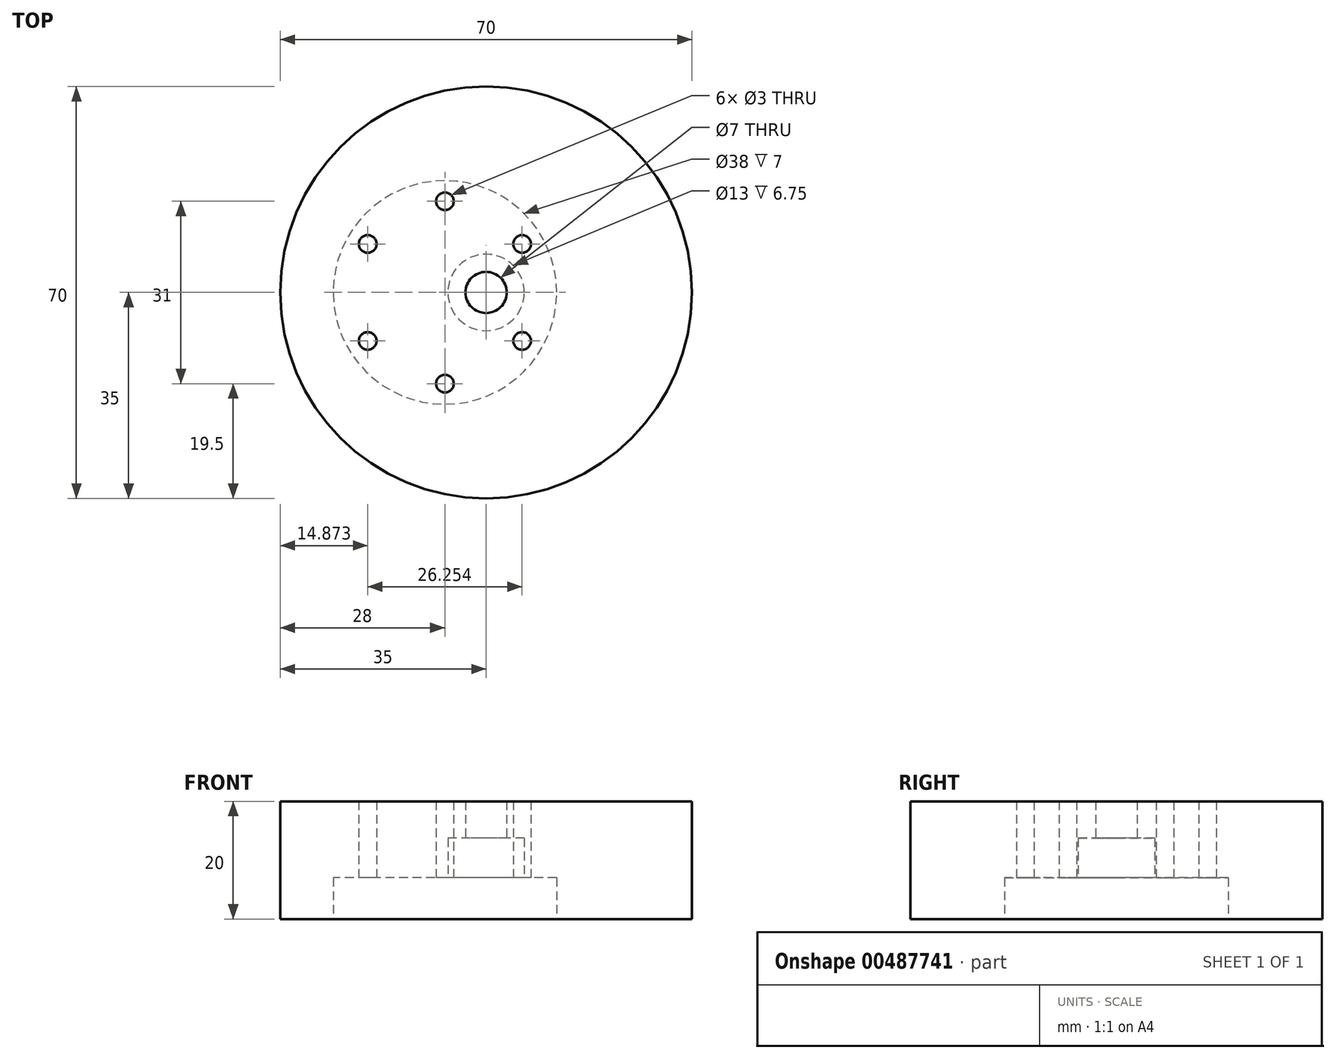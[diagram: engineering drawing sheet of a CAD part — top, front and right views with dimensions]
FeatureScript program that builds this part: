
annotation { "Feature Type Name" : "Feature", "Feature Type Description" : "" }
export const myFeature = defineFeature(function(context is Context, id is Id, definition is map)
    precondition{}
    {
        {
            var Q0;
            Q0=qCreatedBy(makeId("Top.planeOp"),FACE);
            var sketch = newSketch(context, id + "F0", { "sketchPlane" : qUnion([Q0])});
            skCircle(sketch, "E0", {"center": v(0, 0) * mm, "radius": 6.5 * mm});
            skCircle(sketch, "E1", {"center": v(-7, 0) * mm, "radius": 19 * mm});
            skLineSegment(sketch, "E2", {"start": v(-7, 0) * mm, "end": v(0, 0) * mm, "construction": true});
            skCircle(sketch, "E3", {"center": v(0, 0) * mm, "radius": 3.5 * mm});
            skLineSegment(sketch, "E4", {"start": v(-7, 0) * mm, "end": v(-26, 0) * mm, "construction": true});
            skLineSegment(sketch, "E5", {"start": v(-7, -19) * mm, "end": v(-7, 19) * mm, "construction": true});
            skCircle(sketch, "E6", {"center": v(-7, 15.5) * mm, "radius": 1.5 * mm});
            skCircle(sketch, "E7", {"center": v(-7, -15.5) * mm, "radius": 1.5 * mm});
            skCircle(sketch, "E8", {"center": v(-7, 0) * mm, "radius": 15.5 * mm, "construction": true});
            skCircle(sketch, "E9", {"center": v(-20.13, 8.24) * mm, "radius": 1.5 * mm});
            skCircle(sketch, "E10", {"center": v(6.13, -8.24) * mm, "radius": 1.5 * mm});
            skCircle(sketch, "E11", {"center": v(-20.13, -8.24) * mm, "radius": 1.5 * mm});
            skCircle(sketch, "E12", {"center": v(6.13, 8.24) * mm, "radius": 1.5 * mm});
            skLineSegment(sketch, "E13", {"start": v(-20.13, 8.24) * mm, "end": v(6.13, 8.24) * mm, "construction": true});
            skLineSegment(sketch, "E14", {"start": v(-20.13, -8.24) * mm, "end": v(6.13, -8.24) * mm, "construction": true});
            skCircle(sketch, "E15", {"center": v(0, 0) * mm, "radius": 35 * mm});
            skSolve(sketch);
        }
        {
            var Q0;
            Q0=makeQuery(id+"F0.imprint","IMPRINT",FACE,{"disambiguationData":[TD([[makeQuery(id+"F0.imprint","IMPRINT",EDGE,{"derivedFrom":sQuery(id+"F0.wireOp",EDGE,"E1")}),-1.0]])]});
            var Q1;
            Q1=makeQuery(id+"F0.imprint","IMPRINT",FACE,{"disambiguationData":[TD([[makeQuery(id+"F0.imprint","IMPRINT",EDGE,{"derivedFrom":sQuery(id+"F0.wireOp",EDGE,"E0")}),-1.0]])]});
            var Q2;
            Q2=makeQuery(id+"F0.imprint","IMPRINT",FACE,{"disambiguationData":[TD([[makeQuery(id+"F0.imprint","IMPRINT",EDGE,{"derivedFrom":sQuery(id+"F0.wireOp",EDGE,"E0")}),1.0]])]});
            extrude(context, id + "F1", {"entities" : qUnion([Q0, Q1, Q2]), "depth" : 20 * mm});
        }
        {
            var Q0;
            Q0=makeQuery(id+"F0.imprint","IMPRINT",FACE,{"disambiguationData":[TD([[makeQuery(id+"F0.imprint","IMPRINT",EDGE,{"derivedFrom":sQuery(id+"F0.wireOp",EDGE,"E0")}),-1.0]])]});
            extrude(context, id + "F2", {"entities" : qUnion([Q0]), "operationType" : NewBodyOperationType.REMOVE, "depth" : 7 * mm});
        }
        {
            var Q0;
            Q0=makeQuery(id+"F2.boolean.opBoolean","SPLIT",FACE,{"disambiguationData":[TD([makeQuery(id+"F2.opExtrude","SWEPT_FACE",FACE,{"disambiguationData":[OSD([sQuery(id+"F0.wireOp",EDGE,"E0")])]})])],"derivedFrom":makeQuery(id+"F1.opExtrude","CAP_FACE",FACE,{"disambiguationData":[OSD([sQuery(id+"F0.wireOp",EDGE,"E6"),sQuery(id+"F0.wireOp",EDGE,"E7"),sQuery(id+"F0.wireOp",EDGE,"E9"),sQuery(id+"F0.wireOp",EDGE,"E10"),sQuery(id+"F0.wireOp",EDGE,"E11"),sQuery(id+"F0.wireOp",EDGE,"E12"),sQuery(id+"F0.wireOp",EDGE,"E15")])],"isStart":true})});
            extrude(context, id + "F3", {"entities" : qUnion([Q0]), "operationType" : NewBodyOperationType.REMOVE, "oppositeDirection" : true, "depth" : 13.75 * mm});
        }
    });
